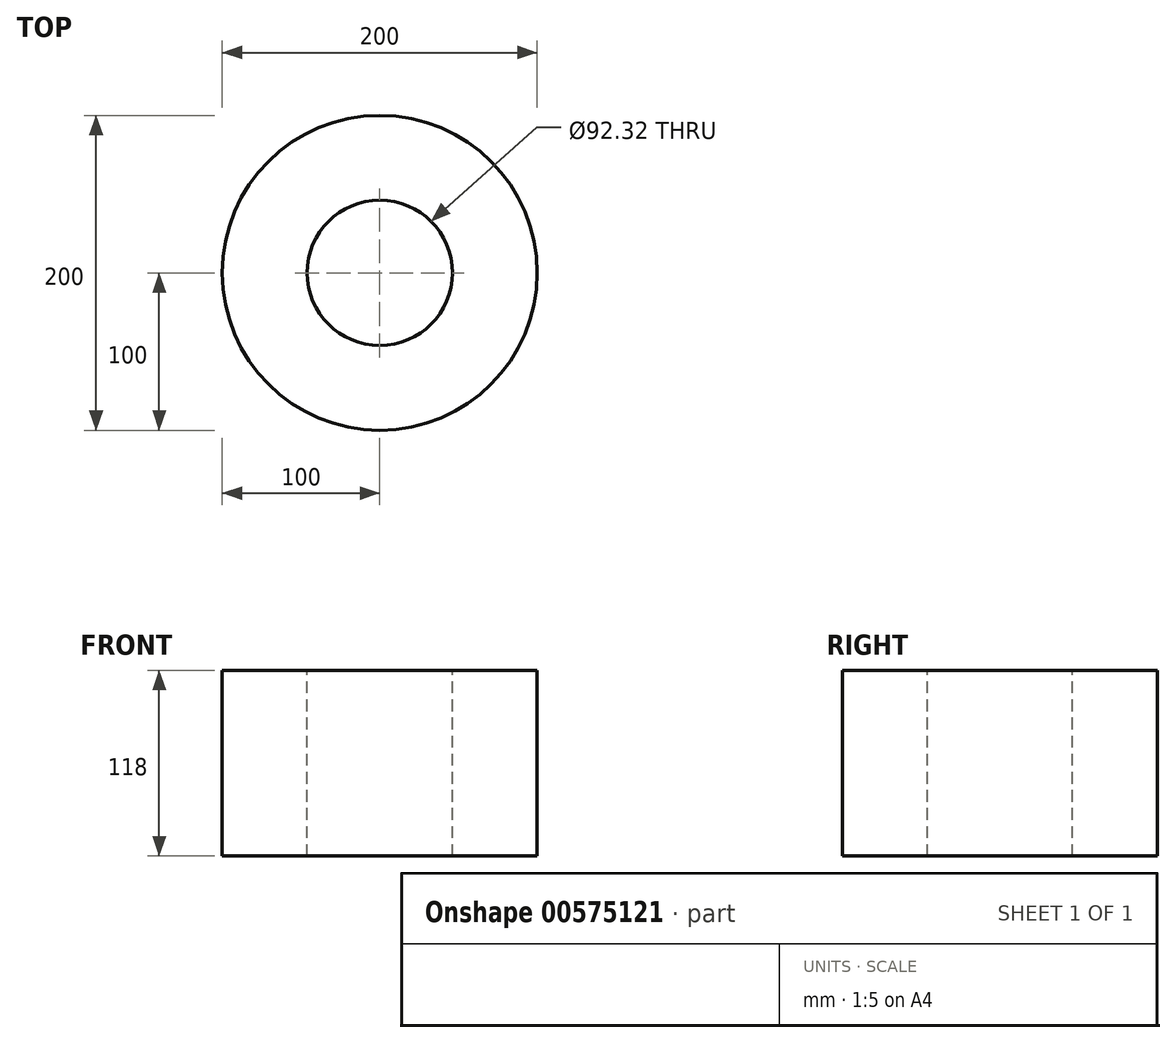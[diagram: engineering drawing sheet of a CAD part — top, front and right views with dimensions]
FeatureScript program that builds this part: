
annotation { "Feature Type Name" : "Feature", "Feature Type Description" : "" }
export const myFeature = defineFeature(function(context is Context, id is Id, definition is map)
    precondition{}
    {
        {
            var Q0;
            Q0=qCreatedBy(makeId("Top.planeOp"),FACE);
            var sketch = newSketch(context, id + "F0", { "sketchPlane" : qUnion([Q0])});
            skCircle(sketch, "E0", {"center": v(0, 0) * mm, "radius": 100 * mm});
            skSolve(sketch);
        }
        {
            var Q0;
            Q0=makeQuery(id+"F0.imprint","IMPRINT",FACE,{"disambiguationData":[TD([[makeQuery(id+"F0.imprint","IMPRINT",EDGE,{"derivedFrom":sQuery(id+"F0.wireOp",EDGE,"E0")}),1.0]])]});
            extrude(context, id + "F1", {"entities" : qUnion([Q0]), "endBound" : BoundingType.SYMMETRIC, "depth" : 118 * mm, "offsetDistance" : 25 * mm});
        }
        {
            var Q0;
            Q0=makeQuery(id+"F1.opExtrude","CAP_FACE",FACE,{"disambiguationData":[OSD([sQuery(id+"F0.wireOp",EDGE,"E0")])],"isStart":false});
            var sketch = newSketch(context, id + "F2", { "sketchPlane" : qUnion([Q0])});
            skCircle(sketch, "E1", {"center": v(0, 0) * mm, "radius": 46.16 * mm});
            skSolve(sketch);
        }
        {
            var Q0;
            Q0=makeQuery(id+"F2.imprint","IMPRINT",FACE,{"disambiguationData":[TD([[makeQuery(id+"F2.imprint","IMPRINT",EDGE,{"derivedFrom":sQuery(id+"F2.wireOp",EDGE,"E1")}),1.0]])]});
            extrude(context, id + "F3", {"entities" : qUnion([Q0]), "operationType" : NewBodyOperationType.REMOVE, "oppositeDirection" : true, "depth" : 155 * mm, "offsetDistance" : 25 * mm});
        }
    });
